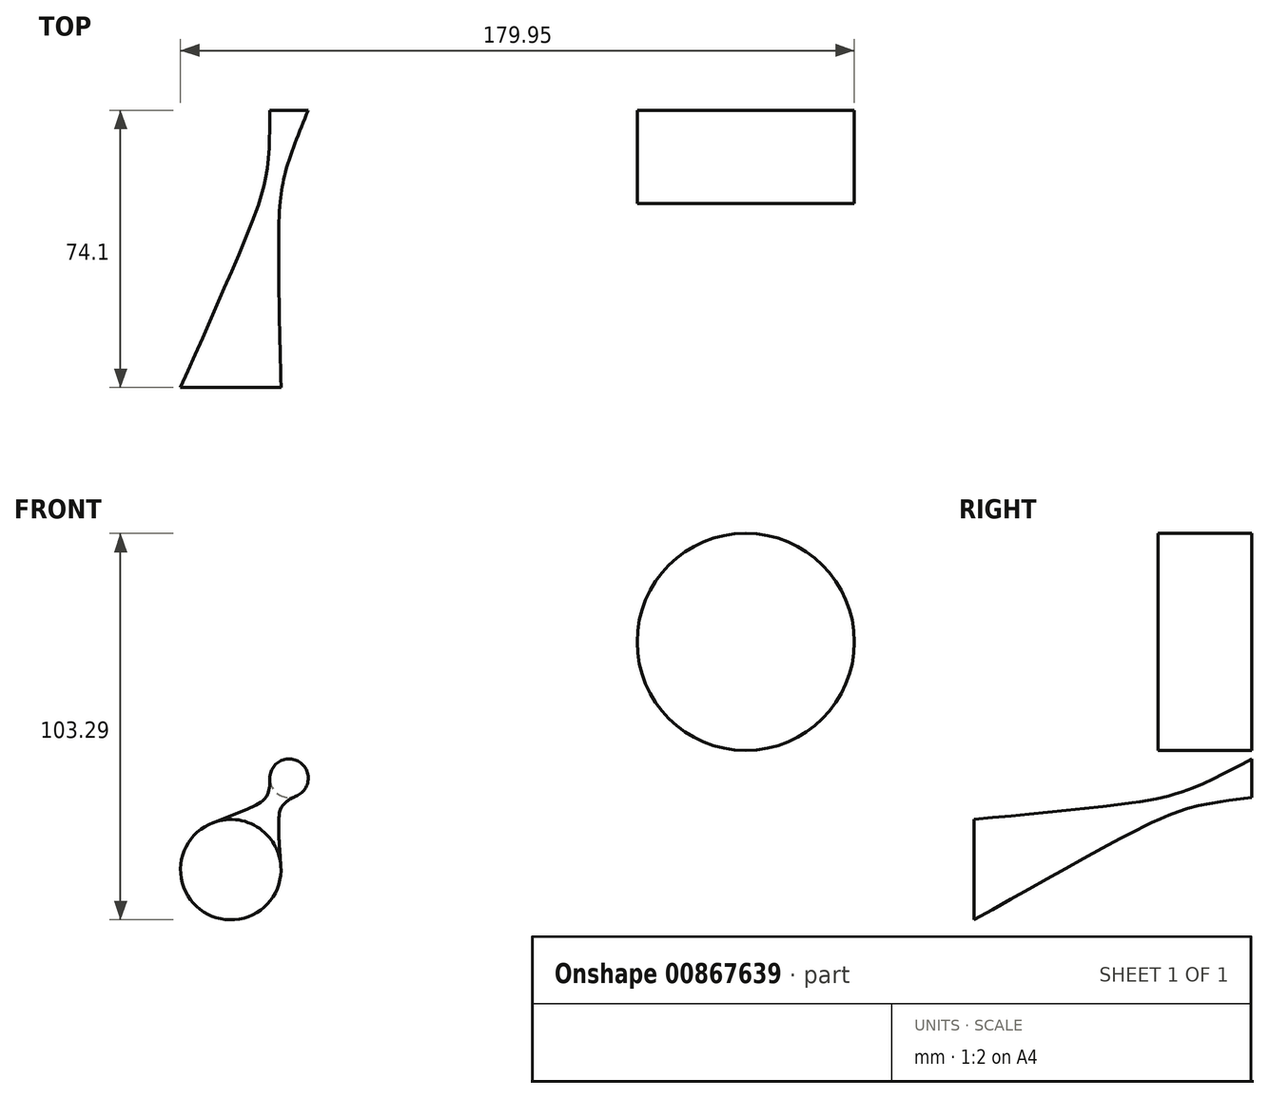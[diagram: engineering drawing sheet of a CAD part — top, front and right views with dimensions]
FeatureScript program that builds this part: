
annotation { "Feature Type Name" : "Feature", "Feature Type Description" : "" }
export const myFeature = defineFeature(function(context is Context, id is Id, definition is map)
    precondition{}
    {
        {
            var Q0;
            Q0=qCreatedBy(makeId("Front.planeOp"),FACE);
            var sketch = newSketch(context, id + "F0", { "sketchPlane" : qUnion([Q0])});
            skCircle(sketch, "E0", {"center": v(-83.32, 28.9) * mm, "radius": 5.13 * mm});
            skCircle(sketch, "E1", {"center": v(-48.56, 69.62) * mm, "radius": 11.8 * mm});
            skSolve(sketch);
        }
        {
            var Q0;
            Q0=qCreatedBy(makeId("Front.planeOp"),FACE);
            cPlane(context, id + "F1", {"entities" : qUnion([Q0]), "cplaneType" : CPlaneType.OFFSET, "offset" : 74.1 * mm, "width" : 150 * mm, "height" : 150 * mm});
        }
        {
            var Q0;
            Q0=qCreatedBy(id+"F1.planeOp",FACE);
            var sketch = newSketch(context, id + "F2", { "sketchPlane" : qUnion([Q0])});
            skCircle(sketch, "E2", {"center": v(-98.89, 4.46) * mm, "radius": 13.42 * mm});
            skSolve(sketch);
        }
        {
            var Q0;
            Q0=makeQuery(id+"F0.imprint","IMPRINT",FACE,{"disambiguationData":[TD([[makeQuery(id+"F0.imprint","IMPRINT",EDGE,{"derivedFrom":sQuery(id+"F0.wireOp",EDGE,"E0")}),1.0]])]});
            var Q1;
            Q1=makeQuery(id+"F2.imprint","IMPRINT",FACE,{"disambiguationData":[TD([[makeQuery(id+"F2.imprint","IMPRINT",EDGE,{"derivedFrom":sQuery(id+"F2.wireOp",EDGE,"E2")}),1.0]])]});
            loft(context, id + "F3", {"sheetProfilesArray" : [{ "sheetProfileEntities" : qUnion([Q0]) }, { "sheetProfileEntities" : qUnion([Q1]) }]});
        }
        {
            var Q0;
            Q0=qCreatedBy(makeId("Front.planeOp"),FACE);
            var sketch = newSketch(context, id + "F4", { "sketchPlane" : qUnion([Q0])});
            skCircle(sketch, "E3", {"center": v(38.64, 65.33) * mm, "radius": 29 * mm});
            skSolve(sketch);
        }
        {
            var Q0;
            Q0 = qSketchRegion(id + "F4", true);
            extrude(context, id + "F5", {"entities" : qUnion([Q0]), "depth" : 25 * mm, "offsetDistance" : 25 * mm});
        }
    });
